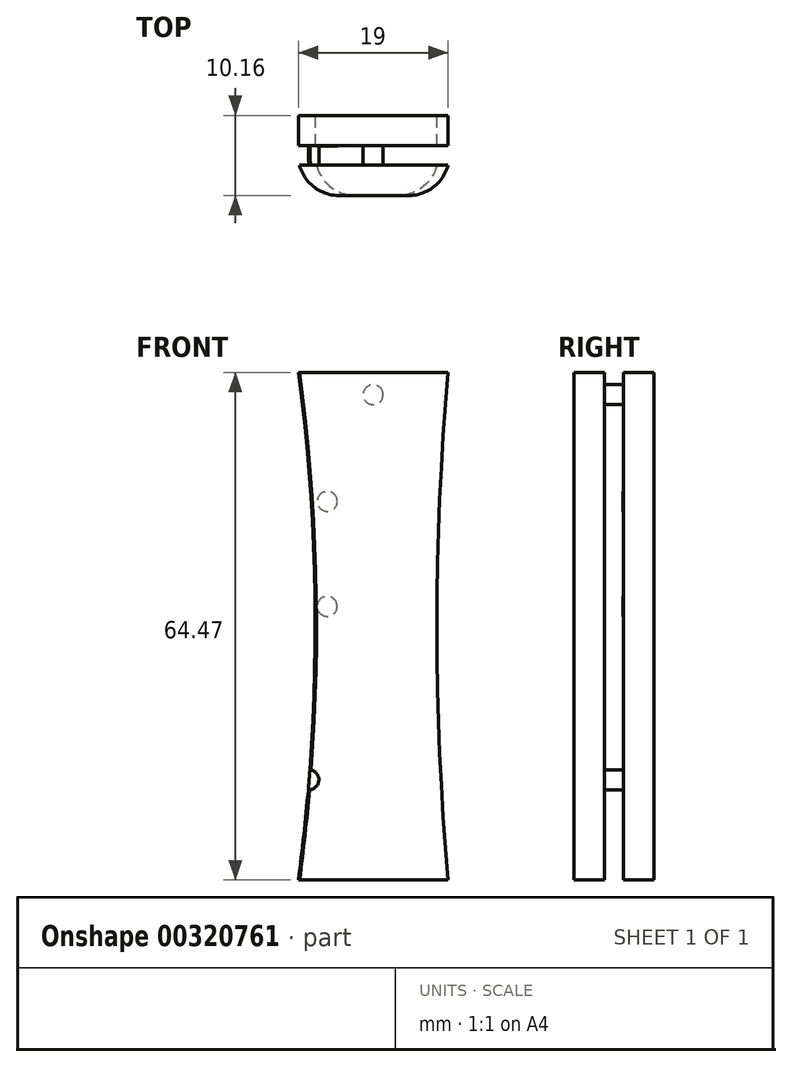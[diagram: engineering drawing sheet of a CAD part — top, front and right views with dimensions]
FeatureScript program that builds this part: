
annotation { "Feature Type Name" : "Feature", "Feature Type Description" : "" }
export const myFeature = defineFeature(function(context is Context, id is Id, definition is map)
    precondition{}
    {
        {
            var Q0;
            Q0=qCreatedBy(makeId("Front.planeOp"),FACE);
            var sketch = newSketch(context, id + "F0", { "sketchPlane" : qUnion([Q0])});
            skLineSegment(sketch, "E0", {"start": v(-9.5, 0) * mm, "end": v(-9.5, -64.47) * mm});
            skLineSegment(sketch, "E1", {"start": v(-9.5, -64.47) * mm, "end": v(0, -64.47) * mm});
            skLineSegment(sketch, "E2", {"start": v(0, -64.47) * mm, "end": v(0, 0) * mm});
            skLineSegment(sketch, "E3", {"start": v(0, 0) * mm, "end": v(-9.5, 0) * mm});
            skLineSegment(sketch, "E4.MirrorCS", {"start": v(0, 0) * mm, "end": v(9.5, 0) * mm});
            skLineSegment(sketch, "E5.MirrorCS", {"start": v(9.5, 0) * mm, "end": v(9.5, -64.47) * mm});
            skLineSegment(sketch, "E6.MirrorCS", {"start": v(9.5, -64.47) * mm, "end": v(0, -64.47) * mm});
            skSolve(sketch);
        }
        {
            var Q0;
            Q0 = qSketchRegion(id + "F0", true);
            extrude(context, id + "F1", {"entities" : qUnion([Q0]), "endBound" : BoundingType.SYMMETRIC, "depth" : 10.16 * mm});
        }
        {
            var Q0;
            Q0=makeQuery(id+"F1.opExtrude","SWEPT_FACE",FACE,{"disambiguationData":[OSD([sQuery(id+"F0.wireOp",EDGE,"E5.MirrorCS")])]});
            var sketch = newSketch(context, id + "F2", { "sketchPlane" : qUnion([Q0])});
            skLineSegment(sketch, "E7", {"start": v(-1.23, 0) * mm, "end": v(-1.23, -64.47) * mm});
            skLineSegment(sketch, "E8", {"start": v(-1.23, -64.47) * mm, "end": v(0, -64.47) * mm});
            skLineSegment(sketch, "E9", {"start": v(0, -64.47) * mm, "end": v(0, 0) * mm});
            skLineSegment(sketch, "E10", {"start": v(0, 0) * mm, "end": v(-1.23, 0) * mm});
            skLineSegment(sketch, "E11.MirrorCS", {"start": v(0, 0) * mm, "end": v(1.23, 0) * mm});
            skLineSegment(sketch, "E12.MirrorCS", {"start": v(1.23, 0) * mm, "end": v(1.23, -64.47) * mm});
            skLineSegment(sketch, "E13.MirrorCS", {"start": v(1.23, -64.47) * mm, "end": v(0, -64.47) * mm});
            skSolve(sketch);
        }
        {
            var Q0;
            Q0 = qSketchRegion(id + "F2", true);
            extrude(context, id + "F3", {"entities" : qUnion([Q0]), "operationType" : NewBodyOperationType.REMOVE, "oppositeDirection" : true, "depth" : 25.4 * mm});
        }
        {
            var Q0;
            Q0=makeQuery(id+"F1.opExtrude","CAP_FACE",FACE,{"disambiguationData":[OSD([sQuery(id+"F0.wireOp",EDGE,"E0"),sQuery(id+"F0.wireOp",EDGE,"E1"),sQuery(id+"F0.wireOp",EDGE,"E3"),sQuery(id+"F0.wireOp",EDGE,"E4.MirrorCS"),sQuery(id+"F0.wireOp",EDGE,"E5.MirrorCS"),sQuery(id+"F0.wireOp",EDGE,"E6.MirrorCS")])],"isStart":true});
            var sketch = newSketch(context, id + "F4", { "sketchPlane" : qUnion([Q0])});
            skCircle(sketch, "E14", {"center": v(8.16, -51.73) * mm, "radius": 1.27 * mm});
            skCircle(sketch, "E15", {"center": v(5.84, -29.7) * mm, "radius": 1.27 * mm});
            skCircle(sketch, "E16", {"center": v(5.82, -16.36) * mm, "radius": 1.27 * mm});
            skCircle(sketch, "E17", {"center": v(0, -2.82) * mm, "radius": 1.27 * mm});
            skSolve(sketch);
        }
        {
            var Q0;
            Q0 = qSketchRegion(id + "F4", true);
            var Q1;
            Q1=makeQuery(id+"F1.opExtrude","CAP_FACE",FACE,{"disambiguationData":[OSD([sQuery(id+"F0.wireOp",EDGE,"E0"),sQuery(id+"F0.wireOp",EDGE,"E1"),sQuery(id+"F0.wireOp",EDGE,"E3"),sQuery(id+"F0.wireOp",EDGE,"E4.MirrorCS"),sQuery(id+"F0.wireOp",EDGE,"E5.MirrorCS"),sQuery(id+"F0.wireOp",EDGE,"E6.MirrorCS")])],"isStart":false});
            extrude(context, id + "F5", {"entities" : qUnion([Q0]), "operationType" : NewBodyOperationType.ADD, "endBound" : BoundingType.UP_TO_SURFACE, "oppositeDirection" : true, "endBoundEntityFace" : qUnion([Q1]), "depth" : 25.4 * mm});
        }
        {
            var Q0;
            Q0=makeQuery(id+"F1.opExtrude","CAP_FACE",FACE,{"disambiguationData":[OSD([sQuery(id+"F0.wireOp",EDGE,"E0"),sQuery(id+"F0.wireOp",EDGE,"E1"),sQuery(id+"F0.wireOp",EDGE,"E3"),sQuery(id+"F0.wireOp",EDGE,"E4.MirrorCS"),sQuery(id+"F0.wireOp",EDGE,"E5.MirrorCS"),sQuery(id+"F0.wireOp",EDGE,"E6.MirrorCS")])],"isStart":true});
            var sketch = newSketch(context, id + "F6", { "sketchPlane" : qUnion([Q0])});
            skArc(sketch, "E18", {"start": v(-9.5, -64.47) * mm, "mid": v(-8.11, -32.23) * mm, "end": v(-9.5, 0) * mm});
            skArc(sketch, "E19", {"start": v(9.5, 0) * mm, "mid": v(7.35, -32.23) * mm, "end": v(9.5, -64.47) * mm});
            skLineSegment(sketch, "E20", {"start": v(-9.5, 0) * mm, "end": v(-9.5, -64.47) * mm});
            skLineSegment(sketch, "E21", {"start": v(9.5, 0) * mm, "end": v(9.5, -64.47) * mm});
            skSolve(sketch);
        }
        {
            var Q0;
            Q0 = qSketchRegion(id + "F6", true);
            extrude(context, id + "F7", {"entities" : qUnion([Q0]), "operationType" : NewBodyOperationType.REMOVE, "oppositeDirection" : true, "depth" : 25.4 * mm});
        }
        {
            var Q0;
            Q0=qCreatedBy(makeId("Right.planeOp"),FACE);
            var sketch = newSketch(context, id + "F8", { "sketchPlane" : qUnion([Q0])});
            skLineSegment(sketch, "E22", {"start": v(1.18, -11.05) * mm, "end": v(1.18, -35.13) * mm});
            skLineSegment(sketch, "E23", {"start": v(-1.22, -11.05) * mm, "end": v(-1.22, -35.13) * mm});
            skLineSegment(sketch, "E24", {"start": v(-1.22, -35.13) * mm, "end": v(1.18, -35.13) * mm});
            skLineSegment(sketch, "E25", {"start": v(1.18, -11.05) * mm, "end": v(-1.22, -11.05) * mm});
            skSolve(sketch);
        }
        {
            var Q0;
            Q0 = qSketchRegion(id + "F8", true);
            extrude(context, id + "F9", {"entities" : qUnion([Q0]), "operationType" : NewBodyOperationType.REMOVE, "oppositeDirection" : true, "depth" : 25.4 * mm});
        }
        {
            var Q0;
            Q0=makeQuery(id+"F7.boolean.opBoolean","COPY",EDGE,{"derivedFrom":makeQuery(id+"F7.opExtrude","CAP_EDGE",EDGE,{"disambiguationData":[OSD([sQuery(id+"F6.wireOp",EDGE,"E18")])],"isStart":true})});
            var Q1;
            Q1=makeQuery(id+"F7.boolean.opBoolean","COPY",EDGE,{"derivedFrom":makeQuery(id+"F7.opExtrude","CAP_EDGE",EDGE,{"disambiguationData":[OSD([sQuery(id+"F6.wireOp",EDGE,"E19")])],"isStart":true})});
            var Q2;
            Q2=makeQuery(id+"F7.boolean.opBoolean","INTERSECT",EDGE,{"derivedFrom":[makeQuery(id+"F1.opExtrude","CAP_FACE",FACE,{"disambiguationData":[OSD([sQuery(id+"F0.wireOp",EDGE,"E0"),sQuery(id+"F0.wireOp",EDGE,"E1"),sQuery(id+"F0.wireOp",EDGE,"E3"),sQuery(id+"F0.wireOp",EDGE,"E4.MirrorCS"),sQuery(id+"F0.wireOp",EDGE,"E5.MirrorCS"),sQuery(id+"F0.wireOp",EDGE,"E6.MirrorCS")])],"isStart":false}),makeQuery(id+"F7.opExtrude","SWEPT_FACE",FACE,{"disambiguationData":[OSD([sQuery(id+"F6.wireOp",EDGE,"E18")])]})]});
            var Q3;
            Q3=makeQuery(id+"F7.boolean.opBoolean","INTERSECT",EDGE,{"derivedFrom":[makeQuery(id+"F1.opExtrude","CAP_FACE",FACE,{"disambiguationData":[OSD([sQuery(id+"F0.wireOp",EDGE,"E0"),sQuery(id+"F0.wireOp",EDGE,"E1"),sQuery(id+"F0.wireOp",EDGE,"E3"),sQuery(id+"F0.wireOp",EDGE,"E4.MirrorCS"),sQuery(id+"F0.wireOp",EDGE,"E5.MirrorCS"),sQuery(id+"F0.wireOp",EDGE,"E6.MirrorCS")])],"isStart":false}),makeQuery(id+"F7.opExtrude","SWEPT_FACE",FACE,{"disambiguationData":[OSD([sQuery(id+"F6.wireOp",EDGE,"E19")])]})]});
            fillet(context, id + "F10", {"entities" : qUnion([Q0, Q1, Q2, Q3]), "radius" : 5.08 * mm, "tangentPropagation" : true, "allowEdgeOverflow" : false});
        }
    });
